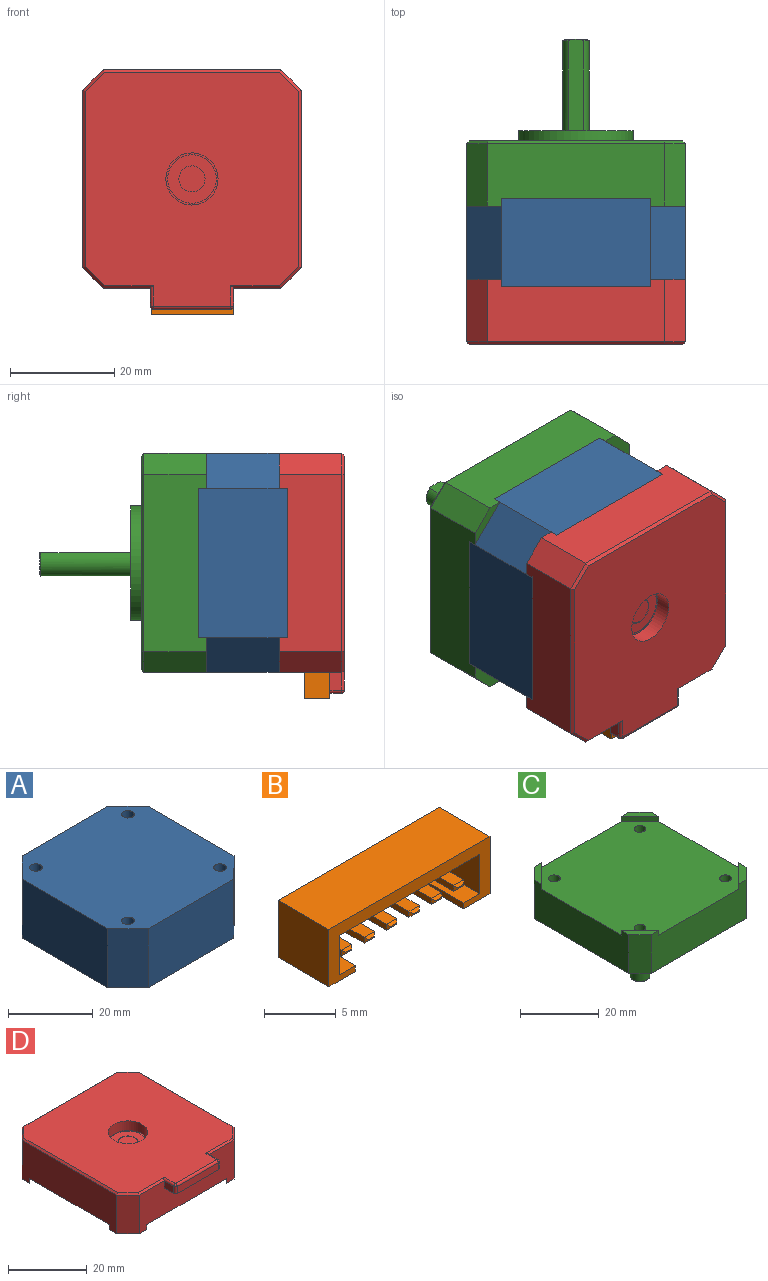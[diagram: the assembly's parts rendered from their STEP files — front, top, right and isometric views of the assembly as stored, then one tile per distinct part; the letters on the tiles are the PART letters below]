
ASSEMBLY  parts=4 mates=9
PART A: 14 faces, bbox 42x42x17 mm
  f0: plane 17x6.69mm, normal (0.71,0.71,0), area 160.8mm2, adj f1,f10,f12,f13
  f1: plane 28.63x17mm, normal (0,1,0), area 486.6mm2, adj f0,f2,f12,f13
  f2: plane 17x6.69mm, normal (-0.71,0.71,0), area 160.8mm2, adj f1,f3,f12,f13
  f3: plane 28.63x17mm, normal (-1,0,0), area 486.6mm2, adj f2,f4,f12,f13
  f4: plane 17x6.69mm, normal (-0.71,-0.71,0), area 160.8mm2, adj f3,f5,f12,f13
  f5: plane 28.63x17mm, normal (0,-1,0), area 486.6mm2, adj f4,f6,f12,f13
  f6: plane 17x6.69mm, normal (0.71,-0.71,0), area 160.8mm2, adj f5,f10,f12,f13
  f7: cylinder r=1.5mm len=17mm, axis (0,0,-1), area 160.2mm2, adj f12,f13
  f8: cylinder r=1.5mm len=17mm, axis (0,0,-1), area 160.2mm2, adj f12,f13
  f9: cylinder r=1.5mm len=17mm, axis (0,0,-1), area 160.2mm2, adj f12,f13
  f10: plane 28.63x17mm, normal (1,0,0), area 486.6mm2, adj f0,f6,f12,f13
  f11: cylinder r=1.5mm len=17mm, axis (0,0,-1), area 160.2mm2, adj f12,f13
  f12: plane 42x42mm, normal (0,0,1), area 1646.3mm2, adj f0,f1,f2,f3,f4,f5,f6,f7
  f13: plane 42x42mm, normal (0,0,-1), area 1646.3mm2, adj f0,f1,f2,f3,f4,f5,f6,f7
PART B: 68 faces, bbox 15.8x5x4.9 mm
  f0: plane 15.82x5mm, normal (0,0,1), area 79.1mm2, adj f1,f10,f11,f12
  f1: plane 5x4.85mm, normal (-1,0,0), area 24.3mm2, adj f0,f9,f11,f12
  f2: plane 4x0.5mm, normal (1,0,0), area 2mm2, adj f3,f9,f11,f13
  f3: plane 4x1.6mm, normal (0,0,1), area 6.4mm2, adj f2,f4,f11,f13
  f4: plane 4x3.35mm, normal (1,0,0), area 13.4mm2, adj f3,f5,f11,f13
  f5: plane 13.82x4mm, normal (0,0,-1), area 55.3mm2, adj f4,f6,f11,f13
  f6: plane 4x3.35mm, normal (-1,0,0), area 13.4mm2, adj f5,f7,f11,f13
  f7: plane 4x1.6mm, normal (0,0,1), area 6.4mm2, adj f6,f8,f11,f13
  f8: plane 4x0.5mm, normal (-1,0,0), area 2mm2, adj f7,f9,f11,f13
  f9: plane 15.82x5mm, normal (0,0,-1), area 36.6mm2, adj f1,f2,f8,f10,f11,f12,f13
  f10: plane 5x4.85mm, normal (1,0,0), area 24.3mm2, adj f0,f9,f11,f12
  f11: plane 15.82x4.85mm, normal (0,-1,0), area 25.1mm2, adj f0,f1,f2,f3,f4,f5,f6,f7
  f12: plane 15.82x4.85mm, normal (0,1,0), area 76.8mm2, adj f0,f1,f9,f10
  f13: plane 13.82x3.85mm, normal (0,-1,0), area 48.7mm2, adj f2,f3,f4,f5,f6,f7,f8,f9
  f14: plane 3.3x1mm, normal (0,0,1), area 3.3mm2, adj f13,f15,f17,f65
  f15: plane 3.3x0.5mm, normal (-1,0,0), area 1.6mm2, adj f13,f14,f16,f64
  f16: plane 3.3x1mm, normal (0,0,-1), area 3.3mm2, adj f13,f15,f17,f66
  f17: plane 3.3x0.5mm, normal (1,0,0), area 1.6mm2, adj f13,f14,f16,f67
  f18: plane 0.6x0.1mm, normal (0,-1,0), area 0.1mm2, adj f64,f65,f66,f67
  f19: plane 3.3x1mm, normal (0,0,1), area 3.3mm2, adj f13,f20,f22,f61
  f20: plane 3.3x0.5mm, normal (-1,0,0), area 1.6mm2, adj f13,f19,f21,f63
  f21: plane 3.3x1mm, normal (0,0,-1), area 3.3mm2, adj f13,f20,f22,f62
  f22: plane 3.3x0.5mm, normal (1,0,0), area 1.6mm2, adj f13,f19,f21,f60
  f23: plane 0.6x0.1mm, normal (0,-1,0), area 0.1mm2, adj f60,f61,f62,f63
  f24: plane 3.3x1mm, normal (0,0,1), area 3.3mm2, adj f13,f25,f27,f57
  f25: plane 3.3x0.5mm, normal (-1,0,0), area 1.6mm2, adj f13,f24,f26,f59
  f26: plane 3.3x1mm, normal (0,0,-1), area 3.3mm2, adj f13,f25,f27,f58
  f27: plane 3.3x0.5mm, normal (1,0,0), area 1.6mm2, adj f13,f24,f26,f56
  f28: plane 0.6x0.1mm, normal (0,-1,0), area 0.1mm2, adj f56,f57,f58,f59
  f29: plane 3.3x1mm, normal (0,0,1), area 3.3mm2, adj f13,f30,f32,f53
  f30: plane 3.3x0.5mm, normal (-1,0,0), area 1.6mm2, adj f13,f29,f31,f55
  f31: plane 3.3x1mm, normal (0,0,-1), area 3.3mm2, adj f13,f30,f32,f54
  f32: plane 3.3x0.5mm, normal (1,0,0), area 1.6mm2, adj f13,f29,f31,f52
  f33: plane 0.6x0.1mm, normal (0,-1,0), area 0.1mm2, adj f52,f53,f54,f55
  f34: plane 3.3x1mm, normal (0,0,1), area 3.3mm2, adj f13,f35,f37,f49
  f35: plane 3.3x0.5mm, normal (-1,0,0), area 1.6mm2, adj f13,f34,f36,f51
  f36: plane 3.3x1mm, normal (0,0,-1), area 3.3mm2, adj f13,f35,f37,f50
  f37: plane 3.3x0.5mm, normal (1,0,0), area 1.6mm2, adj f13,f34,f36,f48
  f38: plane 0.6x0.1mm, normal (0,-1,0), area 0.1mm2, adj f48,f49,f50,f51
  f39: plane 3.3x1mm, normal (0,0,1), area 3.3mm2, adj f13,f40,f42,f45
  f40: plane 3.3x0.5mm, normal (-1,0,0), area 1.6mm2, adj f13,f39,f41,f47
  f41: plane 3.3x1mm, normal (0,0,-1), area 3.3mm2, adj f13,f40,f42,f46
  f42: plane 3.3x0.5mm, normal (1,0,0), area 1.6mm2, adj f13,f39,f41,f44
  f43: plane 0.6x0.1mm, normal (0,-1,0), area 0.1mm2, adj f44,f45,f46,f47
  f44: plane 0.5x0.2mm, normal (0.71,-0.71,0), area 0.1mm2, adj f42,f43,f45,f46
  f45: plane 1x0.2mm, normal (0,-0.71,0.71), area 0.2mm2, adj f39,f43,f44,f47
  f46: plane 1x0.2mm, normal (0,-0.71,-0.71), area 0.2mm2, adj f41,f43,f44,f47
  f47: plane 0.5x0.2mm, normal (-0.71,-0.71,0), area 0.1mm2, adj f40,f43,f45,f46
  f48: plane 0.5x0.2mm, normal (0.71,-0.71,0), area 0.1mm2, adj f37,f38,f49,f50
  f49: plane 1x0.2mm, normal (0,-0.71,0.71), area 0.2mm2, adj f34,f38,f48,f51
  f50: plane 1x0.2mm, normal (0,-0.71,-0.71), area 0.2mm2, adj f36,f38,f48,f51
  f51: plane 0.5x0.2mm, normal (-0.71,-0.71,0), area 0.1mm2, adj f35,f38,f49,f50
  f52: plane 0.5x0.2mm, normal (0.71,-0.71,0), area 0.1mm2, adj f32,f33,f53,f54
  f53: plane 1x0.2mm, normal (0,-0.71,0.71), area 0.2mm2, adj f29,f33,f52,f55
  f54: plane 1x0.2mm, normal (0,-0.71,-0.71), area 0.2mm2, adj f31,f33,f52,f55
  f55: plane 0.5x0.2mm, normal (-0.71,-0.71,0), area 0.1mm2, adj f30,f33,f53,f54
  f56: plane 0.5x0.2mm, normal (0.71,-0.71,0), area 0.1mm2, adj f27,f28,f57,f58
  f57: plane 1x0.2mm, normal (0,-0.71,0.71), area 0.2mm2, adj f24,f28,f56,f59
  f58: plane 1x0.2mm, normal (0,-0.71,-0.71), area 0.2mm2, adj f26,f28,f56,f59
  f59: plane 0.5x0.2mm, normal (-0.71,-0.71,0), area 0.1mm2, adj f25,f28,f57,f58
  f60: plane 0.5x0.2mm, normal (0.71,-0.71,0), area 0.1mm2, adj f22,f23,f61,f62
  f61: plane 1x0.2mm, normal (0,-0.71,0.71), area 0.2mm2, adj f19,f23,f60,f63
  f62: plane 1x0.2mm, normal (0,-0.71,-0.71), area 0.2mm2, adj f21,f23,f60,f63
  f63: plane 0.5x0.2mm, normal (-0.71,-0.71,0), area 0.1mm2, adj f20,f23,f61,f62
  f64: plane 0.5x0.2mm, normal (-0.71,-0.71,0), area 0.1mm2, adj f15,f18,f65,f66
  f65: plane 1x0.2mm, normal (0,-0.71,0.71), area 0.2mm2, adj f14,f18,f64,f67
  f66: plane 1x0.2mm, normal (0,-0.71,-0.71), area 0.2mm2, adj f16,f18,f64,f67
  f67: plane 0.5x0.2mm, normal (0.71,-0.71,0), area 0.1mm2, adj f17,f18,f65,f66
PART C: 41 faces, bbox 42x42x32 mm
  f0: plane 34x12mm, normal (1,0,0), area 365.1mm2, adj f5,f6,f11,f12,f21,f36,f38,f39
  f1: plane 34x12mm, normal (0,1,0), area 365.1mm2, adj f6,f7,f12,f13,f20,f36,f37,f38
  f2: plane 34x12mm, normal (-1,0,0), area 365.1mm2, adj f4,f7,f13,f14,f16,f36,f37,f40
  f3: plane 34x12mm, normal (0,-1,0), area 365.1mm2, adj f4,f5,f11,f14,f17,f36,f39,f40
  f4: plane 6.69x6.69mm, normal (0,0,1), area 14.4mm2, adj f2,f3,f14,f40
  f5: plane 6.69x6.69mm, normal (0,0,1), area 14.4mm2, adj f0,f3,f11,f39
  f6: plane 6.69x6.69mm, normal (0,0,1), area 14.4mm2, adj f0,f1,f12,f38
  f7: plane 6.69x6.69mm, normal (0,0,1), area 14.4mm2, adj f1,f2,f13,f37
  f8: plane 9.5x9.5mm, normal (0,0,-1), area 51.2mm2, adj f26,f27
  f9: plane 28x28mm, normal (0,0,-1), area 235.6mm2, adj f23,f25
  f10: plane 41x41mm, normal (0,0,-1), area 964.7mm2, adj f15,f16,f17,f18,f19,f20,f21,f22
  f11: plane 12x4mm, normal (0.71,-0.71,0), area 67.9mm2, adj f0,f3,f5,f19
  f12: plane 12x4mm, normal (0.71,0.71,0), area 67.9mm2, adj f0,f1,f6,f22
  f13: plane 12x4mm, normal (-0.71,0.71,0), area 67.9mm2, adj f1,f2,f7,f18
  f14: plane 12x4mm, normal (-0.71,-0.71,0), area 67.9mm2, adj f2,f3,f4,f15
  f15: plane 4.21x4.21mm, normal (-0.5,-0.5,-0.71), area 3.9mm2, adj f10,f14,f16,f17
  f16: plane 34x0.5mm, normal (-0.71,0,-0.71), area 23.9mm2, adj f2,f10,f15,f18
  f17: plane 34x0.5mm, normal (0,-0.71,-0.71), area 23.9mm2, adj f3,f10,f15,f19
  f18: plane 4.21x4.21mm, normal (-0.5,0.5,-0.71), area 3.9mm2, adj f10,f13,f16,f20
  f19: plane 4.21x4.21mm, normal (0.5,-0.5,-0.71), area 3.9mm2, adj f10,f11,f17,f21
  f20: plane 34x0.5mm, normal (0,0.71,-0.71), area 23.9mm2, adj f1,f10,f18,f22
  f21: plane 34x0.5mm, normal (0.71,0,-0.71), area 23.9mm2, adj f0,f10,f19,f22
  f22: plane 4.21x4.21mm, normal (0.5,0.5,-0.71), area 3.9mm2, adj f10,f12,f20,f21
  f23: cone r=14mm half-angle=45deg, axis (0,0,-1), area 63.3mm2, adj f9,f10
  f24: plane 22x22mm, normal (0,0,-1), area 309.3mm2, adj f25,f26
  f25: cylinder r=11mm len=22mm, axis (0,0,1), area 172.8mm2, adj f9,f24
  f26: cylinder r=4.75mm len=9.5mm, axis (0,0,1), area 74.6mm2, adj f8,f24
  f27: cylinder r=2.5mm len=19.75mm, axis (0,0,1), area 254.7mm2, adj f8,f29,f30,f31
  f28: plane 4.5x4.25mm, normal (0,0,-1), area 15.6mm2, adj f29,f31
  f29: cone r=2.25mm half-angle=45deg, axis (0,0,1), area 4.3mm2, adj f27,f28,f31
  f30: plane 3x0.5mm, normal (0,0,-1), area 1mm2, adj f27,f31
  f31: plane 17.53x3.03mm, normal (0,1,0), area 52.4mm2, adj f27,f28,f29,f30
  f32: cylinder r=1.5mm len=11mm, axis (0,0,-1), area 103.7mm2, adj f10,f36
  f33: cylinder r=1.5mm len=11mm, axis (0,0,-1), area 103.7mm2, adj f10,f36
  f34: cylinder r=1.5mm len=11mm, axis (0,0,-1), area 103.7mm2, adj f10,f36
  f35: cylinder r=1.5mm len=11mm, axis (0,0,-1), area 103.7mm2, adj f10,f36
  f36: plane 42x42mm, normal (0,0,1), area 1646.3mm2, adj f0,f1,f2,f3,f32,f33,f34,f35
  f37: plane 6.69x6.69mm, normal (0.71,-0.71,0), area 14.2mm2, adj f1,f2,f7,f36
  f38: plane 6.69x6.69mm, normal (-0.71,-0.71,0), area 14.2mm2, adj f0,f1,f6,f36
  f39: plane 6.69x6.69mm, normal (-0.71,0.71,0), area 14.2mm2, adj f0,f3,f5,f36
  f40: plane 6.69x6.69mm, normal (0.71,0.71,0), area 14.2mm2, adj f2,f3,f4,f36
PART D: 44 faces, bbox 42x46x12.5 mm
  f0: plane 9.6x0.5mm, normal (0,-0.71,0.71), area 6.4mm2, adj f1,f8,f9,f43
  f1: plane 34x12mm, normal (0,-1,0), area 328.3mm2, adj f0,f14,f17,f18,f21,f25,f27,f29
  f2: plane 5x5mm, normal (0,0,1), area 19.6mm2, adj f3
  f3: cylinder r=2.5mm len=5mm, axis (0,0,-1), area 1.6mm2, adj f2,f4
  f4: plane 9.3x9.3mm, normal (0,0,1), area 48.3mm2, adj f3,f5
  f5: cylinder r=4.65mm len=9.3mm, axis (0,0,-1), area 2.9mm2, adj f4,f6
  f6: plane 10x10mm, normal (0,0,1), area 10.6mm2, adj f5,f7
  f7: cylinder r=5mm len=10mm, axis (0,0,1), area 94.2mm2, adj f6,f8
  f8: plane 44.9x41mm, normal (0,0,1), area 1632.7mm2, adj f0,f7,f9,f10,f11,f12,f13,f14
  f9: plane 4.21x4.21mm, normal (-0.5,-0.5,0.71), area 3.9mm2, adj f0,f8,f15,f17
  f10: plane 4.21x4.21mm, normal (0.5,-0.5,0.71), area 3.9mm2, adj f8,f13,f14,f18
  f11: plane 4.21x4.21mm, normal (0.5,0.5,0.71), area 3.9mm2, adj f8,f13,f16,f19
  f12: plane 4.21x4.21mm, normal (-0.5,0.5,0.71), area 3.9mm2, adj f8,f15,f16,f20
  f13: plane 34x0.5mm, normal (0.71,0,0.71), area 23.9mm2, adj f8,f10,f11,f28
  f14: plane 9.6x0.5mm, normal (0,-0.71,0.71), area 6.4mm2, adj f1,f8,f10,f37
  f15: plane 34x0.5mm, normal (-0.71,0,0.71), area 23.9mm2, adj f8,f9,f12,f26
  f16: plane 34x0.5mm, normal (0,0.71,0.71), area 23.9mm2, adj f8,f11,f12,f24
  f17: plane 12x4mm, normal (-0.71,-0.71,0), area 67.9mm2, adj f1,f9,f25,f26
  f18: plane 12x4mm, normal (0.71,-0.71,0), area 67.9mm2, adj f1,f10,f27,f28
  f19: plane 12x4mm, normal (0.71,0.71,0), area 67.9mm2, adj f11,f22,f24,f28
  f20: plane 12x4mm, normal (-0.71,0.71,0), area 67.9mm2, adj f12,f23,f24,f26
  f21: plane 42x42mm, normal (0,0,-1), area 1674.6mm2, adj f1,f24,f26,f28,f29,f30,f31,f32
  f22: plane 6.69x6.69mm, normal (0,0,-1), area 14.4mm2, adj f19,f24,f28,f31
  f23: plane 6.69x6.69mm, normal (0,0,-1), area 14.4mm2, adj f20,f24,f26,f32
  f24: plane 34x12mm, normal (0,1,0), area 365.1mm2, adj f16,f19,f20,f21,f22,f23,f31,f32
  f25: plane 6.69x6.69mm, normal (0,0,-1), area 14.4mm2, adj f1,f17,f26,f29
  f26: plane 34x12mm, normal (-1,0,0), area 365.1mm2, adj f15,f17,f20,f21,f23,f25,f29,f32
  f27: plane 6.69x6.69mm, normal (0,0,-1), area 14.4mm2, adj f1,f18,f28,f30
  f28: plane 34x12mm, normal (1,0,0), area 365.1mm2, adj f13,f18,f19,f21,f22,f27,f30,f31
  f29: plane 6.69x6.69mm, normal (0.71,0.71,0), area 14.2mm2, adj f1,f21,f25,f26
  f30: plane 6.69x6.69mm, normal (-0.71,0.71,0), area 14.2mm2, adj f1,f21,f27,f28
  f31: plane 6.69x6.69mm, normal (-0.71,-0.71,0), area 14.2mm2, adj f21,f22,f24,f28
  f32: plane 6.69x6.69mm, normal (0.71,-0.71,0), area 14.2mm2, adj f21,f23,f24,f26
  f33: plane 16x4mm, normal (0,0,-1), area 63.8mm2, adj f1,f34,f35,f36,f38,f41
  f34: plane 3.4x2.2mm, normal (-1,0,0), area 7.5mm2, adj f1,f33,f41,f43
  f35: plane 3.4x2.2mm, normal (1,0,0), area 7.5mm2, adj f1,f33,f37,f38
  f36: plane 14.8x2.2mm, normal (0,-1,0), area 32.6mm2, adj f33,f38,f40,f41
  f37: cylinder r=0.6mm len=3.9mm, axis (0,1,0), area 3.5mm2, adj f1,f8,f14,f35,f39
  f38: cylinder r=0.6mm len=2.2mm, axis (0,0,-1), area 2.1mm2, adj f33,f35,f36,f39
  f39: sphere r=0.6mm, area 0.6mm2, adj f37,f38,f40
  f40: cylinder r=0.6mm len=14.8mm, axis (1,0,0), area 13.9mm2, adj f8,f36,f39,f42
  f41: cylinder r=0.6mm len=2.2mm, axis (0,0,1), area 2.1mm2, adj f33,f34,f36,f42
  f42: sphere r=0.6mm, area 0.6mm2, adj f40,f41,f43
  f43: cylinder r=0.6mm len=3.9mm, axis (0,-1,0), area 3.5mm2, adj f0,f1,f8,f34,f42
PLACE A rot(axis=(1,0,0),90deg) t=(-26.14,-20.36,15.6)mm
PLACE B rot(axis=(1,0,0),90deg) t=(-26.05,-20.36,15.6)mm
PLACE C rot(axis=(1,0,0),90deg) t=(-26.14,-20.36,15.6)mm
PLACE D rot(axis=(1,0,0),90deg) t=(-26.14,-20.36,15.6)mm
MATE planar D.f24 <-> A.f1  axis (0,0,1) through (-26.14,-53.48,36.6)mm
MATE planar D.f28 <-> A.f10  axis (1,0,0) through (-5.14,-53.48,15.6)mm
MATE planar D.f35 <-> B.f10  axis (1,0,0) through (-18.14,-58.76,-7.1)mm
MATE planar A.f1 <-> C.f1  axis (0,0,1) through (-26.14,-39.86,36.6)mm
MATE planar B.f0 <-> D.f33  axis (0,-1,0) through (-26.05,-56.56,-7.9)mm
MATE planar D.f1 <-> B.f12  axis (0,0,-1) through (-26.14,-53,-5.4)mm
MATE planar D.f28 <-> C.f0  axis (1,0,0) through (-5.14,-48.36,29.91)mm
MATE planar D.f21 <-> A.f12  axis (0,1,0) through (-5.14,-48.36,15.6)mm
MATE planar A.f13 <-> C.f36  axis (0,1,0) through (-26.14,-31.36,15.6)mm
